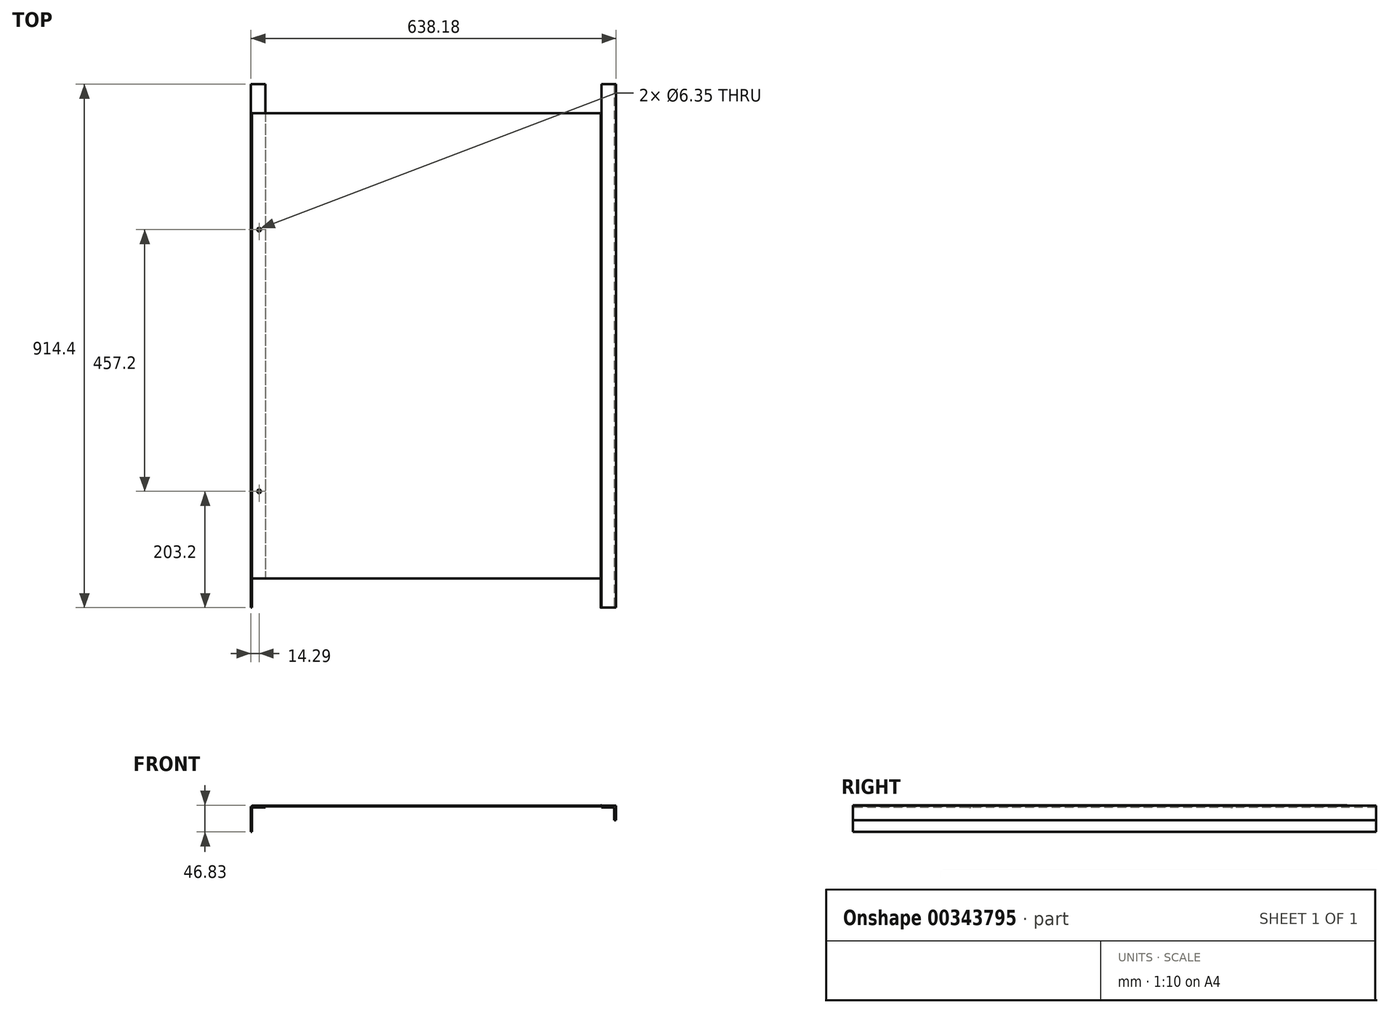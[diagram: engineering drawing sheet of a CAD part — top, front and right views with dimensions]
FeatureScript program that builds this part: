
annotation { "Feature Type Name" : "Feature", "Feature Type Description" : "" }
export const myFeature = defineFeature(function(context is Context, id is Id, definition is map)
    precondition{}
    {
        {
            var Q0;
            Q0=qCreatedBy(makeId("Top.planeOp"),FACE);
            var sketch = newSketch(context, id + "F0", { "sketchPlane" : qUnion([Q0])});
            skLineSegment(sketch, "E0.bottom", {"start": v(304.8, -431.8) * mm, "end": v(-304.8, -431.8) * mm});
            skLineSegment(sketch, "E0.top", {"start": v(304.8, 431.8) * mm, "end": v(-304.8, 431.8) * mm});
            skLineSegment(sketch, "E0.left", {"start": v(304.8, -431.8) * mm, "end": v(304.8, 431.8) * mm});
            skLineSegment(sketch, "E0.right", {"start": v(-304.8, -431.8) * mm, "end": v(-304.8, 431.8) * mm});
            skPoint(sketch, "E0.middle", {"position": v(0, 0) * mm});
            skSolve(sketch);
        }
        {
            var Q0;
            Q0 = qSketchRegion(id + "F0", true);
            extrude(context, id + "F1", {"entities" : qUnion([Q0]), "depth" : 1.59 * mm});
        }
        {
            var Q0;
            Q0=makeQuery(id+"F1.opExtrude","SWEPT_FACE",FACE,{"disambiguationData":[OSD([sQuery(id+"F0.wireOp",EDGE,"E0.bottom")])]});
            var sketch = newSketch(context, id + "F2", { "sketchPlane" : qUnion([Q0])});
            skCircle(sketch, "E1", {"center": v(305.6, 1.59) * mm, "radius": 0.8 * mm});
            skLineSegment(sketch, "E2", {"start": v(306.39, 1.59) * mm, "end": v(331.79, 1.59) * mm});
            skLineSegment(sketch, "E3", {"start": v(331.79, 1.59) * mm, "end": v(331.79, -23.81) * mm});
            skLineSegment(sketch, "E4", {"start": v(331.79, -23.81) * mm, "end": v(328.61, -23.81) * mm});
            skLineSegment(sketch, "E5", {"start": v(328.61, -23.81) * mm, "end": v(328.61, -1.59) * mm});
            skLineSegment(sketch, "E6", {"start": v(328.61, -1.59) * mm, "end": v(306.39, -1.59) * mm});
            skLineSegment(sketch, "E7", {"start": v(306.39, -1.59) * mm, "end": v(306.39, 1.59) * mm});
            skLineSegment(sketch, "E8", {"start": v(304.03, 1.59) * mm, "end": v(307.08, 1.59) * mm, "construction": true});
            skLineSegment(sketch, "E9", {"start": v(-280.99, 0) * mm, "end": v(-306.39, 0) * mm});
            skLineSegment(sketch, "E10", {"start": v(-306.39, 0) * mm, "end": v(-306.39, -44.45) * mm});
            skLineSegment(sketch, "E11", {"start": v(-306.39, -44.45) * mm, "end": v(-304.8, -44.45) * mm});
            skLineSegment(sketch, "E12", {"start": v(-304.8, -44.45) * mm, "end": v(-304.8, -1.59) * mm});
            skLineSegment(sketch, "E13", {"start": v(-304.8, -1.59) * mm, "end": v(-280.99, -1.59) * mm});
            skLineSegment(sketch, "E14", {"start": v(-280.99, -1.59) * mm, "end": v(-280.99, 0) * mm});
            skSolve(sketch);
        }
        {
            var Q0;
            Q0=makeQuery(id+"F2.imprint","IMPRINT",FACE,{"disambiguationData":[TD([[makeQuery(id+"F2.imprint","IMPRINT",EDGE,{"derivedFrom":sQuery(id+"F2.wireOp",EDGE,"E1")}),1.0]])]});
            var Q1;
            Q1=makeQuery(id+"F1.opExtrude","SWEPT_FACE",FACE,{"disambiguationData":[OSD([sQuery(id+"F0.wireOp",EDGE,"E0.top")])]});
            extrude(context, id + "F3", {"entities" : qUnion([Q0]), "endBound" : BoundingType.UP_TO_SURFACE, "oppositeDirection" : true, "endBoundEntityFace" : qUnion([Q1]), "depth" : 25.4 * mm});
        }
        {
            var Q0;
            Q0=makeQuery(id+"F1.opExtrude","CAP_FACE",FACE,{"disambiguationData":[OSD([sQuery(id+"F0.wireOp",EDGE,"E0.bottom"),sQuery(id+"F0.wireOp",EDGE,"E0.top"),sQuery(id+"F0.wireOp",EDGE,"E0.left"),sQuery(id+"F0.wireOp",EDGE,"E0.right")])],"isStart":false});
            var sketch = newSketch(context, id + "F4", { "sketchPlane" : qUnion([Q0])});
            skCircle(sketch, "E15", {"center": v(-292.1, 228.6) * mm, "radius": 3.18 * mm});
            skLineSegment(sketch, "E16", {"start": v(-514.48, 0) * mm, "end": v(-304.8, 0) * mm, "construction": true});
            skCircle(sketch, "E17.MirrorC", {"center": v(-292.1, -228.6) * mm, "radius": 3.18 * mm});
            skSolve(sketch);
        }
        {
            var Q0;
            {var subQ0=sQuery(id+"F2.wireOp",EDGE,"E10");Q0=makeQuery(id+"F2.imprint","IMPRINT",FACE,{"disambiguationData":[TD([[makeQuery(id+"F2.imprint","IMPRINT",EDGE,{"derivedFrom":subQ0}),1.0]])]});}
            var Q1;
            Q1=makeQuery(id+"F2.imprint","IMPRINT",FACE,{"disambiguationData":[TD([[makeQuery(id+"F2.imprint","IMPRINT",EDGE,{"derivedFrom":sQuery(id+"F2.wireOp",EDGE,"E2")}),-1.0]])]});
            extrude(context, id + "F5", {"entities" : qUnion([Q0, Q1]), "operationType" : NewBodyOperationType.ADD, "oppositeDirection" : true, "depth" : 914.4 * mm});
        }
        {
            var Q0;
            Q0 = qSketchRegion(id + "F4", true);
            var Q1;
            Q1=makeQuery(id+"F3.opExtrude","SWEPT_FACE",FACE,{"disambiguationData":[OSD([sQuery(id+"F2.wireOp",EDGE,"E13")])]});
            var Q2;
            Q2=makeQuery(id+"F3.opExtrude","SWEPT_FACE",FACE,{"disambiguationData":[OSD([sQuery(id+"F2.wireOp",EDGE,"E13")])]});
            extrude(context, id + "F6", {"entities" : qUnion([Q0, Q1]), "operationType" : NewBodyOperationType.REMOVE, "oppositeDirection" : true, "endBoundEntityFace" : qUnion([Q2]), "depth" : 25.4 * mm});
        }
        {
            var Q0;
            Q0=makeQuery(id+"F1.opExtrude","CAP_FACE",FACE,{"disambiguationData":[OSD([sQuery(id+"F0.wireOp",EDGE,"E0.bottom"),sQuery(id+"F0.wireOp",EDGE,"E0.top"),sQuery(id+"F0.wireOp",EDGE,"E0.left"),sQuery(id+"F0.wireOp",EDGE,"E0.right")])],"isStart":false});
            var sketch = newSketch(context, id + "F7", { "sketchPlane" : qUnion([Q0])});
            skLineSegment(sketch, "E18.bottom", {"start": v(-304.8, -431.8) * mm, "end": v(306.39, -431.8) * mm});
            skLineSegment(sketch, "E18.top", {"start": v(-304.8, -381) * mm, "end": v(306.39, -381) * mm});
            skLineSegment(sketch, "E18.left", {"start": v(-304.8, -431.8) * mm, "end": v(-304.8, -381) * mm});
            skLineSegment(sketch, "E18.right", {"start": v(306.39, -431.8) * mm, "end": v(306.39, -381) * mm});
            skSolve(sketch);
        }
        {
            var Q0;
            Q0 = qSketchRegion(id + "F7", true);
            extrude(context, id + "F8", {"entities" : qUnion([Q0]), "operationType" : NewBodyOperationType.REMOVE, "oppositeDirection" : true, "depth" : 25.4 * mm});
        }
    });
